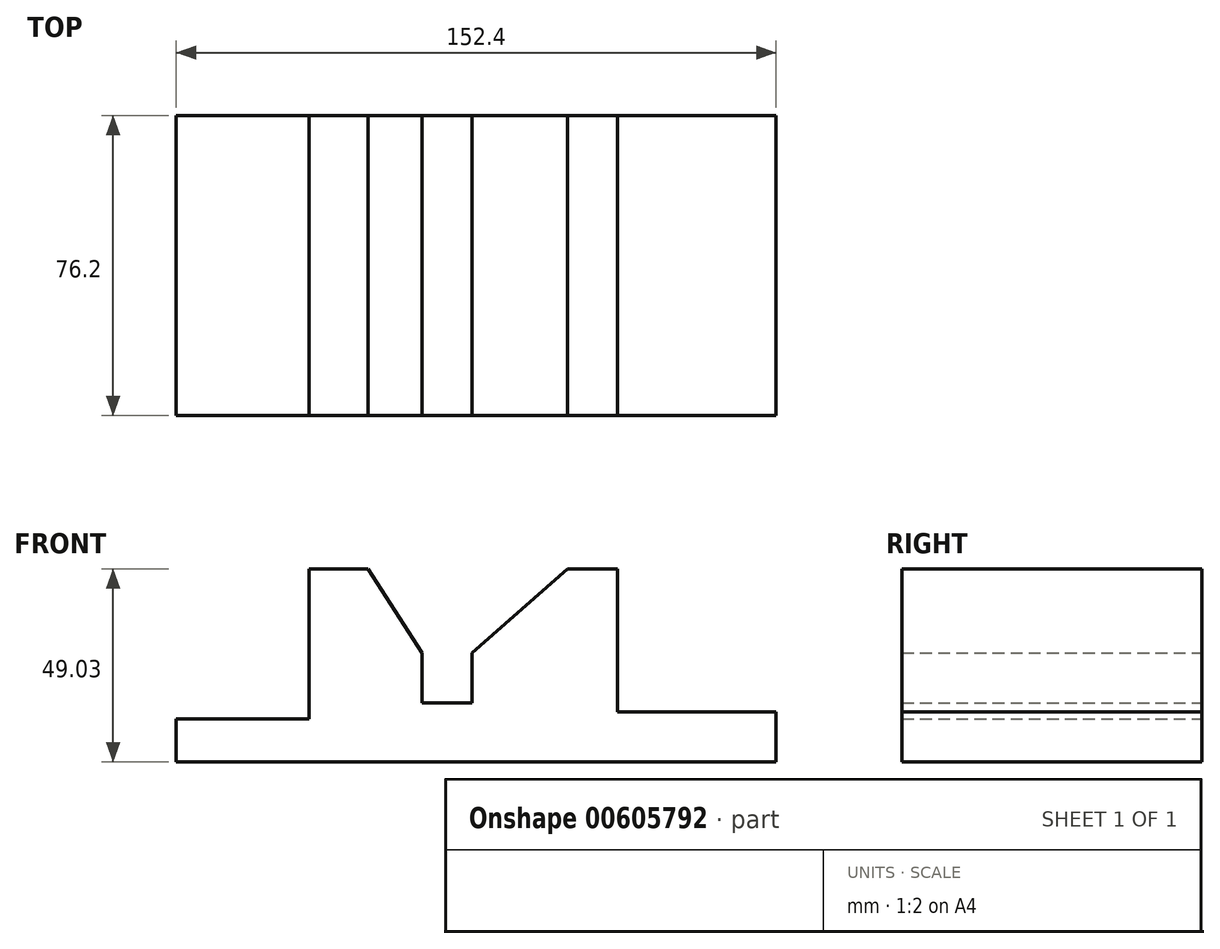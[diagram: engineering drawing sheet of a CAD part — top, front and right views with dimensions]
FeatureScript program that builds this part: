
annotation { "Feature Type Name" : "Feature", "Feature Type Description" : "" }
export const myFeature = defineFeature(function(context is Context, id is Id, definition is map)
    precondition{}
    {
        {
            var Q0;
            Q0=qCreatedBy(makeId("Front.planeOp"),FACE);
            var sketch = newSketch(context, id + "F0", { "sketchPlane" : qUnion([Q0])});
            skLineSegment(sketch, "E0", {"start": v(198.25, 0) * mm, "end": v(350.65, 0) * mm});
            skLineSegment(sketch, "E1", {"start": v(198.25, 0) * mm, "end": v(198.25, 10.93) * mm});
            skLineSegment(sketch, "E2", {"start": v(198.25, 10.93) * mm, "end": v(232, 10.93) * mm});
            skLineSegment(sketch, "E3", {"start": v(232, 10.93) * mm, "end": v(232, 49.03) * mm});
            skLineSegment(sketch, "E4", {"start": v(232, 49.03) * mm, "end": v(246.96, 49.03) * mm});
            skLineSegment(sketch, "E5", {"start": v(246.96, 49.03) * mm, "end": v(260.68, 27.66) * mm});
            skLineSegment(sketch, "E6", {"start": v(260.68, 27.66) * mm, "end": v(260.68, 14.96) * mm});
            skLineSegment(sketch, "E7", {"start": v(260.68, 14.96) * mm, "end": v(273.38, 14.96) * mm});
            skLineSegment(sketch, "E8", {"start": v(273.38, 14.96) * mm, "end": v(273.38, 27.66) * mm});
            skLineSegment(sketch, "E9", {"start": v(350.65, 0) * mm, "end": v(350.65, 12.7) * mm});
            skLineSegment(sketch, "E10", {"start": v(273.38, 27.66) * mm, "end": v(297.7, 49.03) * mm});
            skLineSegment(sketch, "E11", {"start": v(297.7, 49.03) * mm, "end": v(310.4, 49.03) * mm});
            skLineSegment(sketch, "E12", {"start": v(350.65, 12.7) * mm, "end": v(310.4, 12.7) * mm});
            skLineSegment(sketch, "E13", {"start": v(310.4, 49.03) * mm, "end": v(310.4, 12.7) * mm});
            skSolve(sketch);
        }
        {
            var Q0;
            Q0 = qSketchRegion(id + "F0", true);
            extrude(context, id + "F1", {"entities" : qUnion([Q0]), "depth" : 76.2 * mm, "offsetDistance" : 25.4 * mm});
        }
    });
